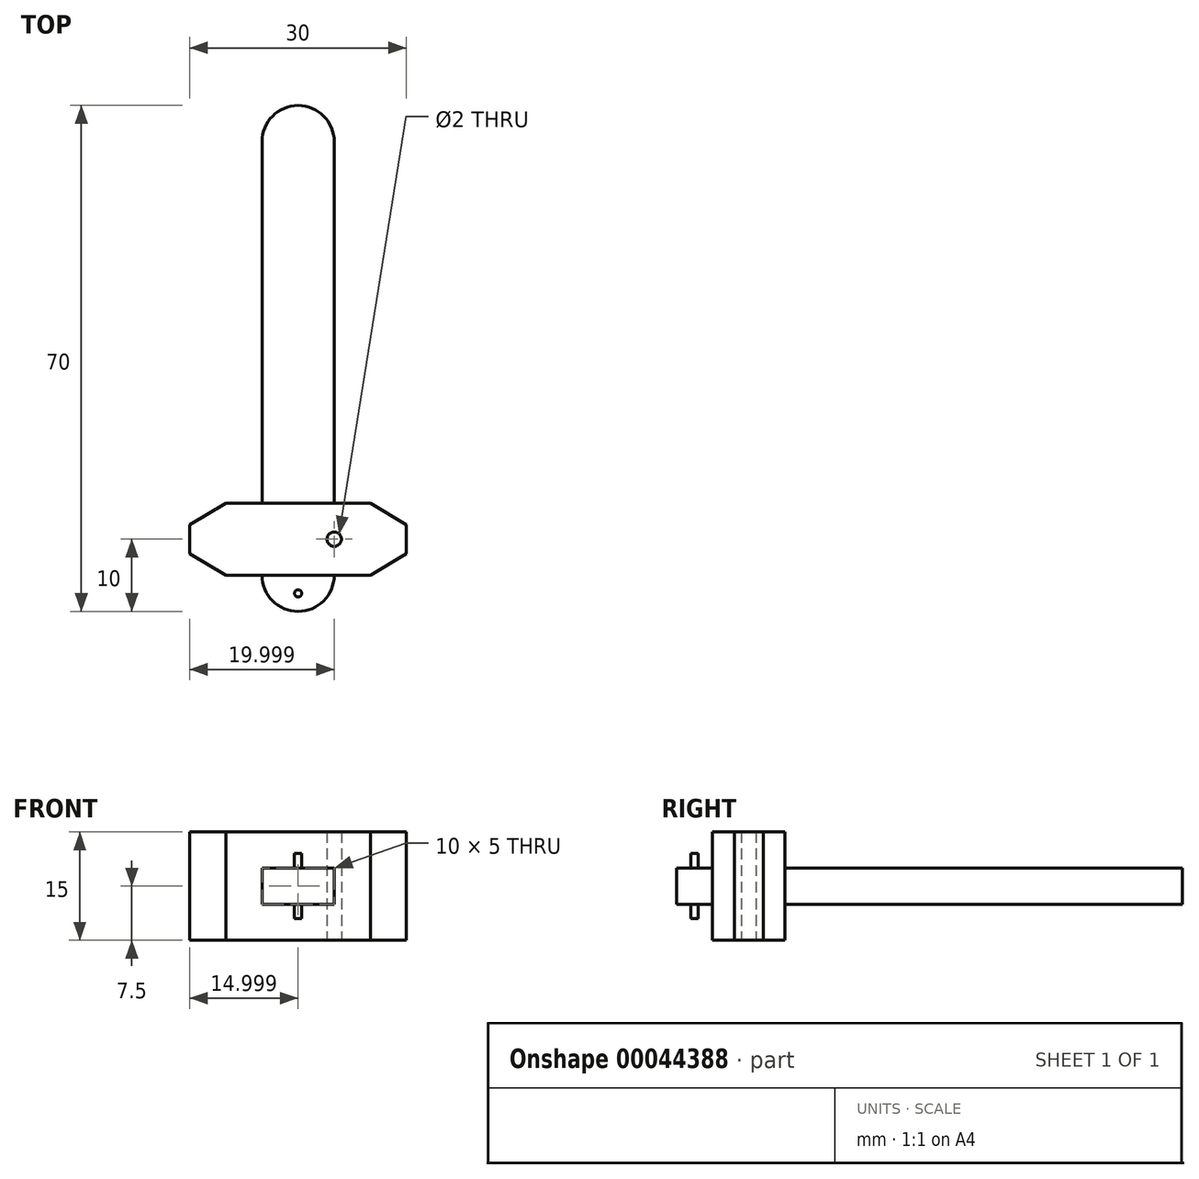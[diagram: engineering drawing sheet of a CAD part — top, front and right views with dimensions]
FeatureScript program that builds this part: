
annotation { "Feature Type Name" : "Feature", "Feature Type Description" : "" }
export const myFeature = defineFeature(function(context is Context, id is Id, definition is map)
    precondition{}
    {
        {
            var Q0;
            Q0=qCreatedBy(makeId("Top.planeOp"),FACE);
            var sketch = newSketch(context, id + "F0", { "sketchPlane" : qUnion([Q0])});
            skLineSegment(sketch, "E0.bottom", {"start": v(-60.48, 10) * mm, "end": v(-50.48, 10) * mm});
            skLineSegment(sketch, "E0.top", {"start": v(-60.48, 0) * mm, "end": v(-50.48, 0) * mm});
            skLineSegment(sketch, "E1.bottom", {"start": v(-60.48, 0) * mm, "end": v(-65.48, 0) * mm});
            skLineSegment(sketch, "E1.top", {"start": v(-60.48, 10) * mm, "end": v(-65.48, 10) * mm});
            skLineSegment(sketch, "E1.right", {"start": v(-70.48, 3) * mm, "end": v(-70.48, 7) * mm});
            skLineSegment(sketch, "E2", {"start": v(-65.48, 0) * mm, "end": v(-70.48, 3) * mm});
            skLineSegment(sketch, "E3", {"start": v(-70.48, 7) * mm, "end": v(-65.48, 10) * mm});
            skLineSegment(sketch, "E4.MirrorCS", {"start": v(-50.48, 10) * mm, "end": v(-45.48, 10) * mm});
            skLineSegment(sketch, "E5.MirrorCS", {"start": v(-40.48, 7) * mm, "end": v(-45.48, 10) * mm});
            skLineSegment(sketch, "E6.MirrorCS", {"start": v(-40.48, 3) * mm, "end": v(-40.48, 7) * mm});
            skLineSegment(sketch, "E7.MirrorCS", {"start": v(-45.48, 0) * mm, "end": v(-40.48, 3) * mm});
            skLineSegment(sketch, "E8.MirrorCS", {"start": v(-50.48, 0) * mm, "end": v(-45.48, 0) * mm});
            skArc(sketch, "E9", {"start": v(-60.48, 0) * mm, "mid": v(-55.48, -5) * mm, "end": v(-50.48, 0) * mm});
            skLineSegment(sketch, "E10", {"start": v(-60.48, 10) * mm, "end": v(-60.48, 60) * mm});
            skLineSegment(sketch, "E11", {"start": v(-50.48, 10) * mm, "end": v(-50.48, 60) * mm});
            skArc(sketch, "E12", {"start": v(-60.48, 60) * mm, "mid": v(-55.48, 65) * mm, "end": v(-50.48, 60) * mm});
            skLineSegment(sketch, "E13", {"start": v(-55.48, 0) * mm, "end": v(-55.48, 10) * mm, "construction": true});
            skLineSegment(sketch, "E14", {"start": v(-50.48, 0) * mm, "end": v(-50.48, -5) * mm, "construction": true});
            skCircle(sketch, "E15", {"center": v(-55.48, -2.5) * mm, "radius": 0.5 * mm});
            skCircle(sketch, "E16", {"center": v(-60.48, 5) * mm, "radius": 1 * mm});
            skPoint(sketch, "E16.centerSnap0", {"position": v(-55.48, 5) * mm});
            skCircle(sketch, "E17.MirrorC", {"center": v(-50.48, 5) * mm, "radius": 1 * mm});
            skLineSegment(sketch, "E18", {"start": v(-55.48, 10) * mm, "end": v(-55.48, 5) * mm, "construction": true});
            skLineSegment(sketch, "E19", {"start": v(21.32, 65) * mm, "end": v(21.32, -5) * mm, "construction": true});
            skPoint(sketch, "E19.startSnap0", {"position": v(-55.48, 65) * mm});
            skLineSegment(sketch, "E20", {"start": v(32.03, 3) * mm, "end": v(32.03, 65) * mm, "construction": true});
            skLineSegment(sketch, "E21", {"start": v(-55.48, 5) * mm, "end": v(-55.48, 0) * mm, "construction": true});
            skSolve(sketch);
        }
        {
            var Q0;
            Q0 = qSketchRegion(id + "F0", true);
            var Q1;
            Q1=makeQuery(id+"F0.imprint","IMPRINT",FACE,{"disambiguationData":[TD([[makeQuery(id+"F0.imprint","IMPRINT",EDGE,{"derivedFrom":sQuery(id+"F0.wireOp",EDGE,"E15")}),1.0]])]});
            extrude(context, id + "F1", {"entities" : qUnion([Q0, Q1]), "depth" : 5 * mm});
        }
        {
            var Q0;
            Q0=makeQuery(id+"F0.imprint","IMPRINT",FACE,{"disambiguationData":[TD([[makeQuery(id+"F0.imprint","IMPRINT",EDGE,{"derivedFrom":sQuery(id+"F0.wireOp",EDGE,"E15")}),1.0]])]});
            extrude(context, id + "F2", {"entities" : qUnion([Q0]), "operationType" : NewBodyOperationType.ADD, "depth" : 7 * mm});
        }
        {
            var Q0;
            Q0=makeQuery(id+"F0.imprint","IMPRINT",FACE,{"disambiguationData":[TD([[makeQuery(id+"F0.imprint","IMPRINT",EDGE,{"derivedFrom":sQuery(id+"F0.wireOp",EDGE,"E15")}),1.0]])]});
            extrude(context, id + "F3", {"entities" : qUnion([Q0]), "operationType" : NewBodyOperationType.ADD, "oppositeDirection" : true, "depth" : 2 * mm});
        }
        {
            var Q0;
            Q0=makeQuery(id+"F0.imprint","IMPRINT",FACE,{"disambiguationData":[TD([[makeQuery(id+"F0.imprint","IMPRINT",EDGE,{"derivedFrom":sQuery(id+"F0.wireOp",EDGE,"E16")}),1.0]])]});
            var Q1;
            Q1=makeQuery(id+"F0.imprint","IMPRINT",FACE,{"disambiguationData":[TD([[makeQuery(id+"F0.imprint","IMPRINT",EDGE,{"derivedFrom":sQuery(id+"F0.wireOp",EDGE,"E17.MirrorC")}),-1.0]])]});
            extrude(context, id + "F4", {"entities" : qUnion([Q0, Q1]), "operationType" : NewBodyOperationType.ADD, "depth" : 10 * mm});
        }
        {
            var Q0;
            Q0=makeQuery(id+"F0.imprint","IMPRINT",FACE,{"disambiguationData":[TD([[makeQuery(id+"F0.imprint","IMPRINT",EDGE,{"derivedFrom":sQuery(id+"F0.wireOp",EDGE,"E17.MirrorC")}),-1.0]])]});
            var Q1;
            Q1=makeQuery(id+"F0.imprint","IMPRINT",FACE,{"disambiguationData":[TD([[makeQuery(id+"F0.imprint","IMPRINT",EDGE,{"derivedFrom":sQuery(id+"F0.wireOp",EDGE,"E16")}),1.0]])]});
            extrude(context, id + "F5", {"entities" : qUnion([Q0, Q1]), "operationType" : NewBodyOperationType.ADD, "oppositeDirection" : true, "depth" : 5 * mm});
        }
    });
